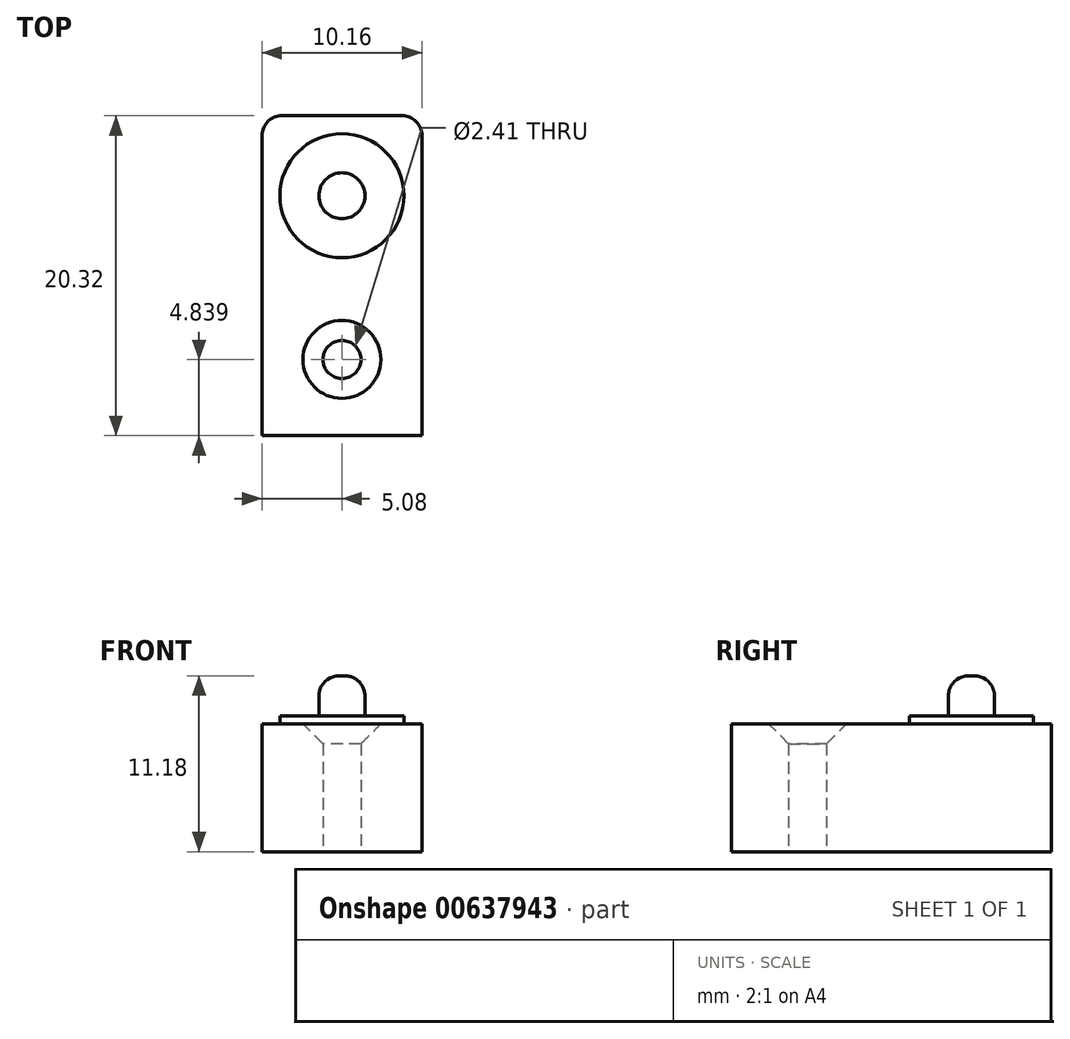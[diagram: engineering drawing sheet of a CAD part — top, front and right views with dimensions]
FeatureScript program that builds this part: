
annotation { "Feature Type Name" : "Feature", "Feature Type Description" : "" }
export const myFeature = defineFeature(function(context is Context, id is Id, definition is map)
    precondition{}
    {
        {
            var Q0;
            Q0=qCreatedBy(makeId("Top.planeOp"),FACE);
            var sketch = newSketch(context, id + "F0", { "sketchPlane" : qUnion([Q0])});
            skLineSegment(sketch, "E0.bottom", {"start": v(5.08, -10.16) * mm, "end": v(-5.08, -10.16) * mm});
            skLineSegment(sketch, "E0.top", {"start": v(3.81, 10.16) * mm, "end": v(-3.8, 10.16) * mm});
            skLineSegment(sketch, "E0.left", {"start": v(5.08, -10.16) * mm, "end": v(5.08, 8.89) * mm});
            skLineSegment(sketch, "E0.right", {"start": v(-5.08, -10.16) * mm, "end": v(-5.08, 8.89) * mm});
            skPoint(sketch, "E0.middle", {"position": v(0, 0) * mm});
            skCircle(sketch, "E1", {"center": v(0, -5.32) * mm, "radius": 1.2 * mm});
            skPoint(sketch, "E2.visualSharp", {"position": v(-5.08, 10.16) * mm});
            skArc(sketch, "E2.filletArc", {"start": v(-3.8, 10.16) * mm, "mid": v(-4.7, 9.79) * mm, "end": v(-5.08, 8.89) * mm});
            skPoint(sketch, "E3.visualSharp", {"position": v(5.08, 10.16) * mm});
            skArc(sketch, "E3.filletArc", {"start": v(5.08, 8.89) * mm, "mid": v(4.7, 9.79) * mm, "end": v(3.81, 10.16) * mm});
            skSolve(sketch);
        }
        {
            var Q0;
            Q0=makeQuery(id+"F0.imprint","IMPRINT",FACE,{"disambiguationData":[TD([[makeQuery(id+"F0.imprint","IMPRINT",EDGE,{"derivedFrom":sQuery(id+"F0.wireOp",EDGE,"E0.bottom")}),-1.0]])]});
            extrude(context, id + "F1", {"entities" : qUnion([Q0]), "depth" : 8.13 * mm, "offsetDistance" : 25.4 * mm});
        }
        {
            var Q0;
            Q0=makeQuery(id+"F1.opExtrude","CAP_EDGE",EDGE,{"disambiguationData":[OSD([sQuery(id+"F0.wireOp",EDGE,"E1")])],"isStart":false});
            chamfer(context, id + "F2", {"entities" : qUnion([Q0]), "width" : 1.27 * mm, "tangentPropagation" : true});
        }
        {
            var Q0;
            Q0=makeQuery(id+"F1.opExtrude","CAP_FACE",FACE,{"disambiguationData":[OSD([sQuery(id+"F0.wireOp",EDGE,"E0.bottom"),sQuery(id+"F0.wireOp",EDGE,"E0.top"),sQuery(id+"F0.wireOp",EDGE,"E0.left"),sQuery(id+"F0.wireOp",EDGE,"E0.right"),sQuery(id+"F0.wireOp",EDGE,"E1"),sQuery(id+"F0.wireOp",EDGE,"E2.filletArc"),sQuery(id+"F0.wireOp",EDGE,"E3.filletArc")])],"isStart":false});
            var sketch = newSketch(context, id + "F3", { "sketchPlane" : qUnion([Q0])});
            skCircle(sketch, "E4", {"center": v(0, 5.08) * mm, "radius": 3.94 * mm});
            skPoint(sketch, "E5", {"position": v(0, -5.32) * mm});
            skSolve(sketch);
        }
        {
            var Q0;
            Q0=makeQuery(id+"F3.imprint","IMPRINT",FACE,{"disambiguationData":[TD([[makeQuery(id+"F3.imprint","IMPRINT",EDGE,{"derivedFrom":sQuery(id+"F3.wireOp",EDGE,"E4")}),1.0]])]});
            extrude(context, id + "F4", {"entities" : qUnion([Q0]), "operationType" : NewBodyOperationType.ADD, "depth" : 0.5 * mm, "offsetDistance" : 25.4 * mm});
        }
        {
            var Q0;
            Q0=makeQuery(id+"F4.opExtrude","CAP_FACE",FACE,{"disambiguationData":[OSD([sQuery(id+"F3.wireOp",EDGE,"E4")])],"isStart":false});
            var sketch = newSketch(context, id + "F5", { "sketchPlane" : qUnion([Q0])});
            skCircle(sketch, "E6", {"center": v(0, 5.08) * mm, "radius": 1.46 * mm});
            skSolve(sketch);
        }
        {
            var Q0;
            Q0=makeQuery(id+"F5.imprint","IMPRINT",FACE,{"disambiguationData":[TD([[makeQuery(id+"F5.imprint","IMPRINT",EDGE,{"derivedFrom":sQuery(id+"F5.wireOp",EDGE,"E6")}),1.0]])]});
            extrude(context, id + "F6", {"entities" : qUnion([Q0]), "operationType" : NewBodyOperationType.ADD, "depth" : 2.54 * mm, "offsetDistance" : 25.4 * mm});
        }
        {
            var Q0;
            Q0=makeQuery(id+"F6.opExtrude","CAP_EDGE",EDGE,{"disambiguationData":[OSD([sQuery(id+"F5.wireOp",EDGE,"E6")])],"isStart":false});
            fillet(context, id + "F7", {"entities" : qUnion([Q0]), "radius" : 1.27 * mm, "tangentPropagation" : true, "allowEdgeOverflow" : false});
        }
    });
